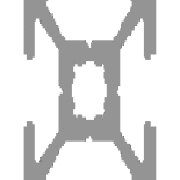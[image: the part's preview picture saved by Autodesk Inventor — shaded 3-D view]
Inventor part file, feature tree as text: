
AUTODESK INVENTOR PART (.ipt)
format: ipt  version: 2021.3 (Build 253353000, 353)  size: 286,208 bytes
history: native  units: mm
features: other x4, sketch x3, extrude x1, plane x1
ambient origin geometry x8: Origin, YZ Plane, XZ Plane, XY Plane, X Axis, Y Axis, Z Axis, Center Point
bodies: Body (feature_tree)
feature tree (9):
  other  "Driven Length"
  other  "Frame Generator"
  extrude  "Extrusion_20x20"  Depth=1.5mm
  other  "Start Plane"
  other  "End Plane"
  sketch  "Sketch"  dims[d7=3.0mm d9=1.5mm d10=0.5mm d13=0.5mm d14=0.5mm d18=3.0mm d19=3.0mm d21=0.5mm d22=0.5mm d23=0.5mm d24=2.75mm d25=1.5mm d26=10.0mm d27=10.0mm d28=3.0mm d29=3.0mm d30=5.5mm d31=1.5mm d32=0.5mm d33=0.5mm d34=0.5mm d35=0.5mm d36=0.5mm d37=0.5mm d38=0.5mm d39=0.5mm d40=0.5mm d41=2.75mm d42=2.75mm d43=0.5mm d44=40.0mm d46=360.0deg d50=-0.0mm d51=200.0mm d52=0.13mm d53=0.0mm d54=90.0deg d55=200.0mm]
  sketch  "Sketch2"  dims[d4=5.5mm d5=1.5mm]
  plane  "Work Plane3"
  sketch  "Sketch3"  dims[d6=1.5mm]
